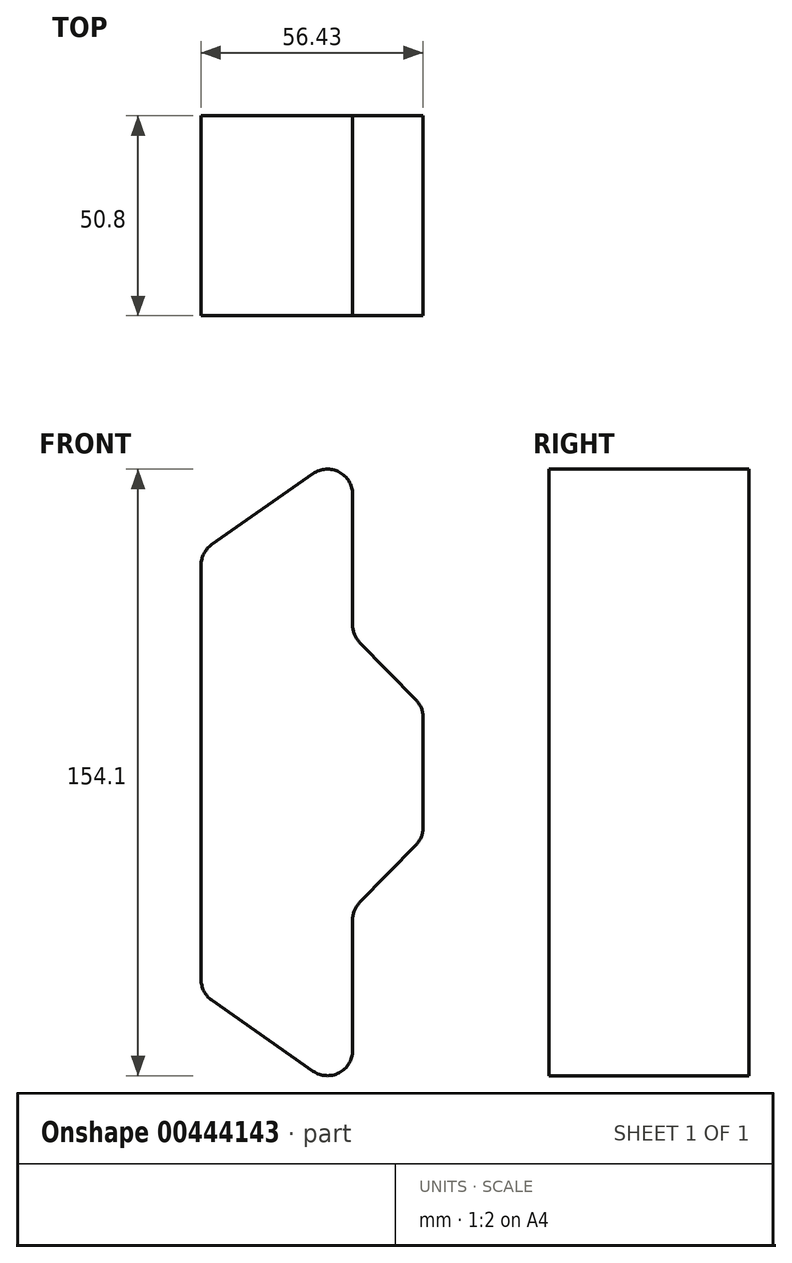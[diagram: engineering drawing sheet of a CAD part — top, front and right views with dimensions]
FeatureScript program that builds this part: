
annotation { "Feature Type Name" : "Feature", "Feature Type Description" : "" }
export const myFeature = defineFeature(function(context is Context, id is Id, definition is map)
    precondition{}
    {
        {
            var Q0;
            Q0=qCreatedBy(makeId("Front.planeOp"),FACE);
            var sketch = newSketch(context, id + "F0", { "sketchPlane" : qUnion([Q0])});
            skLineSegment(sketch, "E0", {"start": v(-29.65, 0) * mm, "end": v(-29.65, -52.65) * mm});
            skLineSegment(sketch, "E1", {"start": v(-26.94, -57.85) * mm, "end": v(-1.16, -75.9) * mm});
            skLineSegment(sketch, "E2", {"start": v(8.83, -70.7) * mm, "end": v(8.83, -37.48) * mm});
            skLineSegment(sketch, "E3", {"start": v(10.64, -33.04) * mm, "end": v(24.97, -18.36) * mm});
            skLineSegment(sketch, "E4", {"start": v(26.78, -13.93) * mm, "end": v(26.78, 0) * mm});
            skPoint(sketch, "E5.visualSharp", {"position": v(-29.65, -55.96) * mm});
            skArc(sketch, "E5.filletArc", {"start": v(-29.65, -52.65) * mm, "mid": v(-28.93, -55.58) * mm, "end": v(-26.94, -57.85) * mm});
            skPoint(sketch, "E6.visualSharp", {"position": v(8.83, -82.9) * mm});
            skArc(sketch, "E6.filletArc", {"start": v(-1.16, -75.9) * mm, "mid": v(5.41, -76.33) * mm, "end": v(8.83, -70.7) * mm});
            skPoint(sketch, "E7.visualSharp", {"position": v(8.83, -34.89) * mm});
            skArc(sketch, "E7.filletArc", {"start": v(10.64, -33.04) * mm, "mid": v(9.3, -35.08) * mm, "end": v(8.83, -37.48) * mm});
            skPoint(sketch, "E8.visualSharp", {"position": v(26.78, -16.51) * mm});
            skArc(sketch, "E8.filletArc", {"start": v(24.97, -18.36) * mm, "mid": v(26.3, -16.32) * mm, "end": v(26.78, -13.93) * mm});
            skLineSegment(sketch, "E9.0", {"start": v(33.13, -13.93) * mm, "end": v(33.13, 0) * mm});
            skArc(sketch, "E9.1", {"start": v(29.51, -22.8) * mm, "mid": v(32.19, -18.72) * mm, "end": v(33.13, -13.93) * mm});
            skLineSegment(sketch, "E9.2", {"start": v(15.18, -37.48) * mm, "end": v(29.51, -22.8) * mm});
            skLineSegment(sketch, "E9.3", {"start": v(15.18, -70.7) * mm, "end": v(15.18, -37.48) * mm});
            skLineSegment(sketch, "E9.4", {"start": v(-36, 0) * mm, "end": v(-36, -52.65) * mm});
            skArc(sketch, "E9.5", {"start": v(-36, -52.65) * mm, "mid": v(-34.57, -58.52) * mm, "end": v(-30.58, -63.05) * mm});
            skLineSegment(sketch, "E9.6", {"start": v(-30.58, -63.05) * mm, "end": v(-4.8, -81.1) * mm});
            skArc(sketch, "E9.7", {"start": v(-4.8, -81.1) * mm, "mid": v(8.34, -81.96) * mm, "end": v(15.18, -70.7) * mm});
            skArc(sketch, "E10.MirrorCS", {"start": v(10.64, 33.04) * mm, "mid": v(9.3, 35.08) * mm, "end": v(8.83, 37.48) * mm});
            skArc(sketch, "E11.MirrorCS", {"start": v(24.97, 18.36) * mm, "mid": v(26.3, 16.32) * mm, "end": v(26.78, 13.93) * mm});
            skArc(sketch, "E12.MirrorCS", {"start": v(-29.65, 52.65) * mm, "mid": v(-28.93, 55.58) * mm, "end": v(-26.94, 57.85) * mm});
            skLineSegment(sketch, "E13.MirrorCS", {"start": v(-36, 0) * mm, "end": v(-36, 52.65) * mm});
            skArc(sketch, "E14.MirrorCS", {"start": v(-36, 52.65) * mm, "mid": v(-34.57, 58.52) * mm, "end": v(-30.58, 63.05) * mm});
            skLineSegment(sketch, "E15.MirrorCS", {"start": v(-30.58, 63.05) * mm, "end": v(-4.8, 81.1) * mm});
            skLineSegment(sketch, "E16.MirrorCS", {"start": v(-29.65, 0) * mm, "end": v(-29.65, 52.65) * mm});
            skLineSegment(sketch, "E17.MirrorCS", {"start": v(-26.94, 57.85) * mm, "end": v(-1.16, 75.9) * mm});
            skPoint(sketch, "E18.MirrorP", {"position": v(8.83, 82.9) * mm});
            skLineSegment(sketch, "E19.MirrorCS", {"start": v(8.83, 70.7) * mm, "end": v(8.83, 37.48) * mm});
            skLineSegment(sketch, "E20.MirrorCS", {"start": v(10.64, 33.04) * mm, "end": v(24.97, 18.36) * mm});
            skLineSegment(sketch, "E21.MirrorCS", {"start": v(26.78, 13.93) * mm, "end": v(26.78, 0) * mm});
            skArc(sketch, "E22.MirrorCS", {"start": v(-1.16, 75.9) * mm, "mid": v(5.41, 76.33) * mm, "end": v(8.83, 70.7) * mm});
            skLineSegment(sketch, "E23.MirrorCS", {"start": v(33.13, 13.93) * mm, "end": v(33.13, 0) * mm});
            skArc(sketch, "E24.MirrorCS", {"start": v(29.51, 22.8) * mm, "mid": v(32.19, 18.72) * mm, "end": v(33.13, 13.93) * mm});
            skLineSegment(sketch, "E25.MirrorCS", {"start": v(15.18, 37.48) * mm, "end": v(29.51, 22.8) * mm});
            skLineSegment(sketch, "E26.MirrorCS", {"start": v(15.18, 70.7) * mm, "end": v(15.18, 37.48) * mm});
            skArc(sketch, "E27.MirrorCS", {"start": v(-4.8, 81.1) * mm, "mid": v(8.34, 81.96) * mm, "end": v(15.18, 70.7) * mm});
            skPoint(sketch, "E28.MirrorP", {"position": v(-29.65, 55.96) * mm});
            skPoint(sketch, "E29.MirrorP", {"position": v(8.83, 34.89) * mm});
            skPoint(sketch, "E30.MirrorP", {"position": v(26.78, 16.51) * mm});
            skSolve(sketch);
        }
        {
            var Q0;
            Q0=makeQuery(id+"F0.imprint","IMPRINT",FACE,{"disambiguationData":[TD([[makeQuery(id+"F0.imprint","IMPRINT",EDGE,{"derivedFrom":sQuery(id+"F0.wireOp",EDGE,"E0")}),1.0]])]});
            extrude(context, id + "F1", {"entities" : qUnion([Q0]), "depth" : 25.4 * mm});
        }
        {
            var Q0;
            Q0=makeQuery(id+"F1.opExtrude","CAP_FACE",FACE,{"disambiguationData":[OSD([sQuery(id+"F0.wireOp",EDGE,"E0"),sQuery(id+"F0.wireOp",EDGE,"E1"),sQuery(id+"F0.wireOp",EDGE,"E2"),sQuery(id+"F0.wireOp",EDGE,"E3"),sQuery(id+"F0.wireOp",EDGE,"E4"),sQuery(id+"F0.wireOp",EDGE,"E5.filletArc"),sQuery(id+"F0.wireOp",EDGE,"E6.filletArc"),sQuery(id+"F0.wireOp",EDGE,"E7.filletArc"),sQuery(id+"F0.wireOp",EDGE,"E8.filletArc"),sQuery(id+"F0.wireOp",EDGE,"E10.MirrorCS"),sQuery(id+"F0.wireOp",EDGE,"E11.MirrorCS"),sQuery(id+"F0.wireOp",EDGE,"E12.MirrorCS"),sQuery(id+"F0.wireOp",EDGE,"E16.MirrorCS"),sQuery(id+"F0.wireOp",EDGE,"E17.MirrorCS"),sQuery(id+"F0.wireOp",EDGE,"E19.MirrorCS"),sQuery(id+"F0.wireOp",EDGE,"E20.MirrorCS"),sQuery(id+"F0.wireOp",EDGE,"E21.MirrorCS"),sQuery(id+"F0.wireOp",EDGE,"E22.MirrorCS")])],"isStart":false});
            extrude(context, id + "F2", {"entities" : qUnion([Q0]), "operationType" : NewBodyOperationType.ADD, "depth" : 25.4 * mm, "offsetDistance" : 25.4 * mm});
        }
    });
